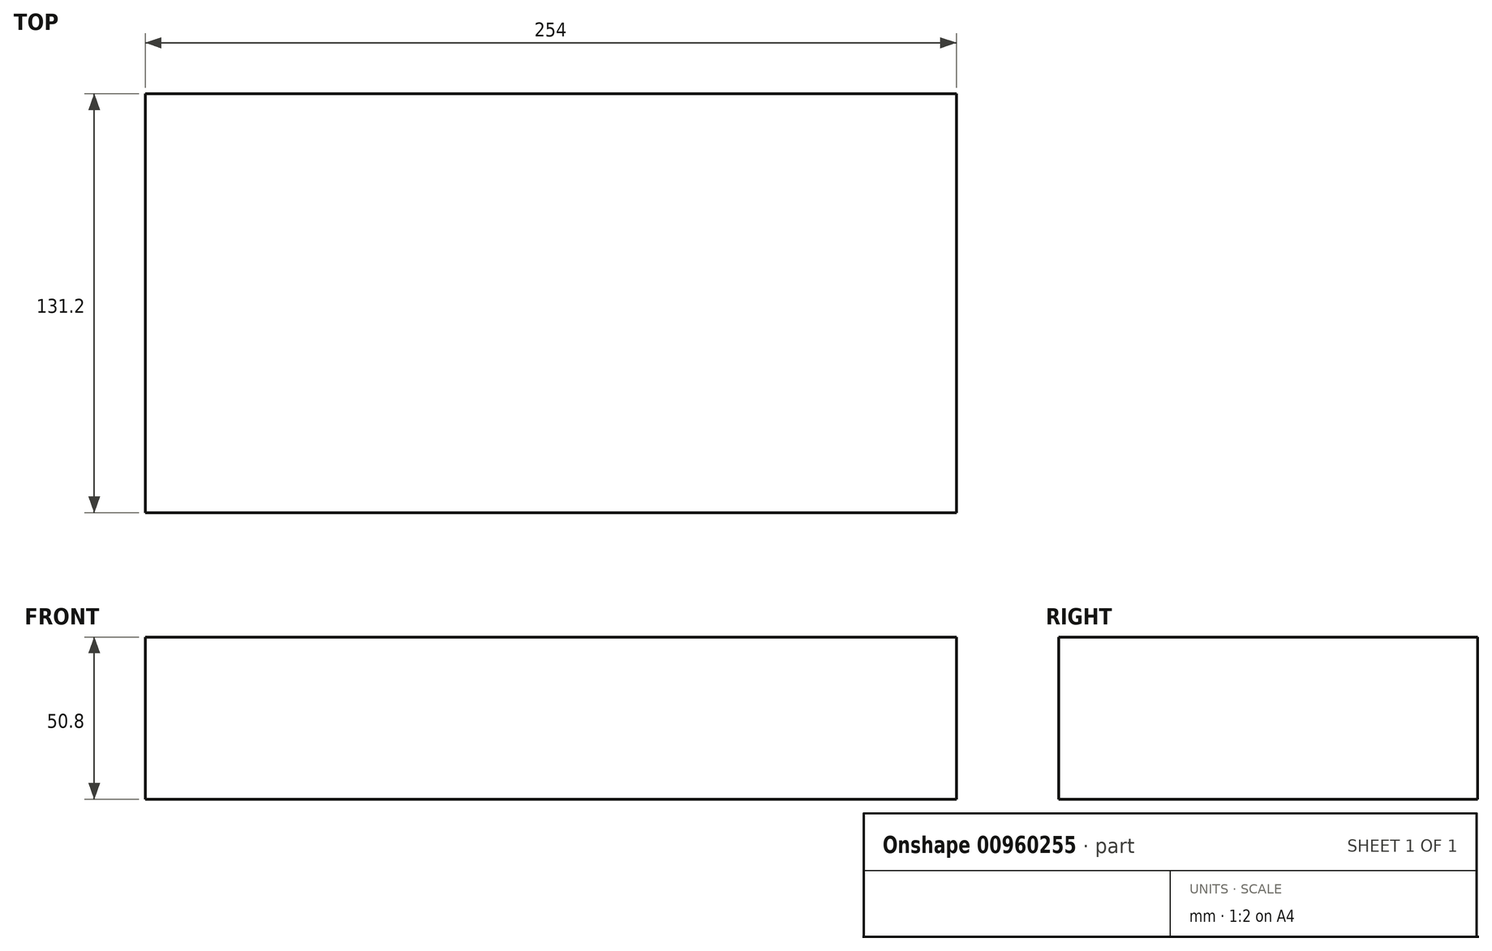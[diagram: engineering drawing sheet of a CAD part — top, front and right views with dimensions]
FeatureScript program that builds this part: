
annotation { "Feature Type Name" : "Feature", "Feature Type Description" : "" }
export const myFeature = defineFeature(function(context is Context, id is Id, definition is map)
    precondition{}
    {
        {
            var Q0;
            Q0=qCreatedBy(makeId("Top.planeOp"),FACE);
            var sketch = newSketch(context, id + "F0", { "sketchPlane" : qUnion([Q0])});
            skLineSegment(sketch, "E0.bottom", {"start": v(-127, 65.6) * mm, "end": v(127, 65.6) * mm});
            skLineSegment(sketch, "E0.top", {"start": v(-127, -65.6) * mm, "end": v(127, -65.6) * mm});
            skLineSegment(sketch, "E0.left", {"start": v(-127, 65.6) * mm, "end": v(-127, -65.6) * mm});
            skLineSegment(sketch, "E0.right", {"start": v(127, 65.6) * mm, "end": v(127, -65.6) * mm});
            skPoint(sketch, "E0.middle", {"position": v(0, 0) * mm});
            skSolve(sketch);
        }
        {
            var Q0;
            Q0=makeQuery(id+"F0.imprint","IMPRINT",FACE,{"disambiguationData":[TD([[makeQuery(id+"F0.imprint","IMPRINT",EDGE,{"derivedFrom":sQuery(id+"F0.wireOp",EDGE,"E0.bottom")}),-1.0]])]});
            extrude(context, id + "F1", {"entities" : qUnion([Q0]), "depth" : 50.8 * mm, "offsetDistance" : 25.4 * mm});
        }
    });
